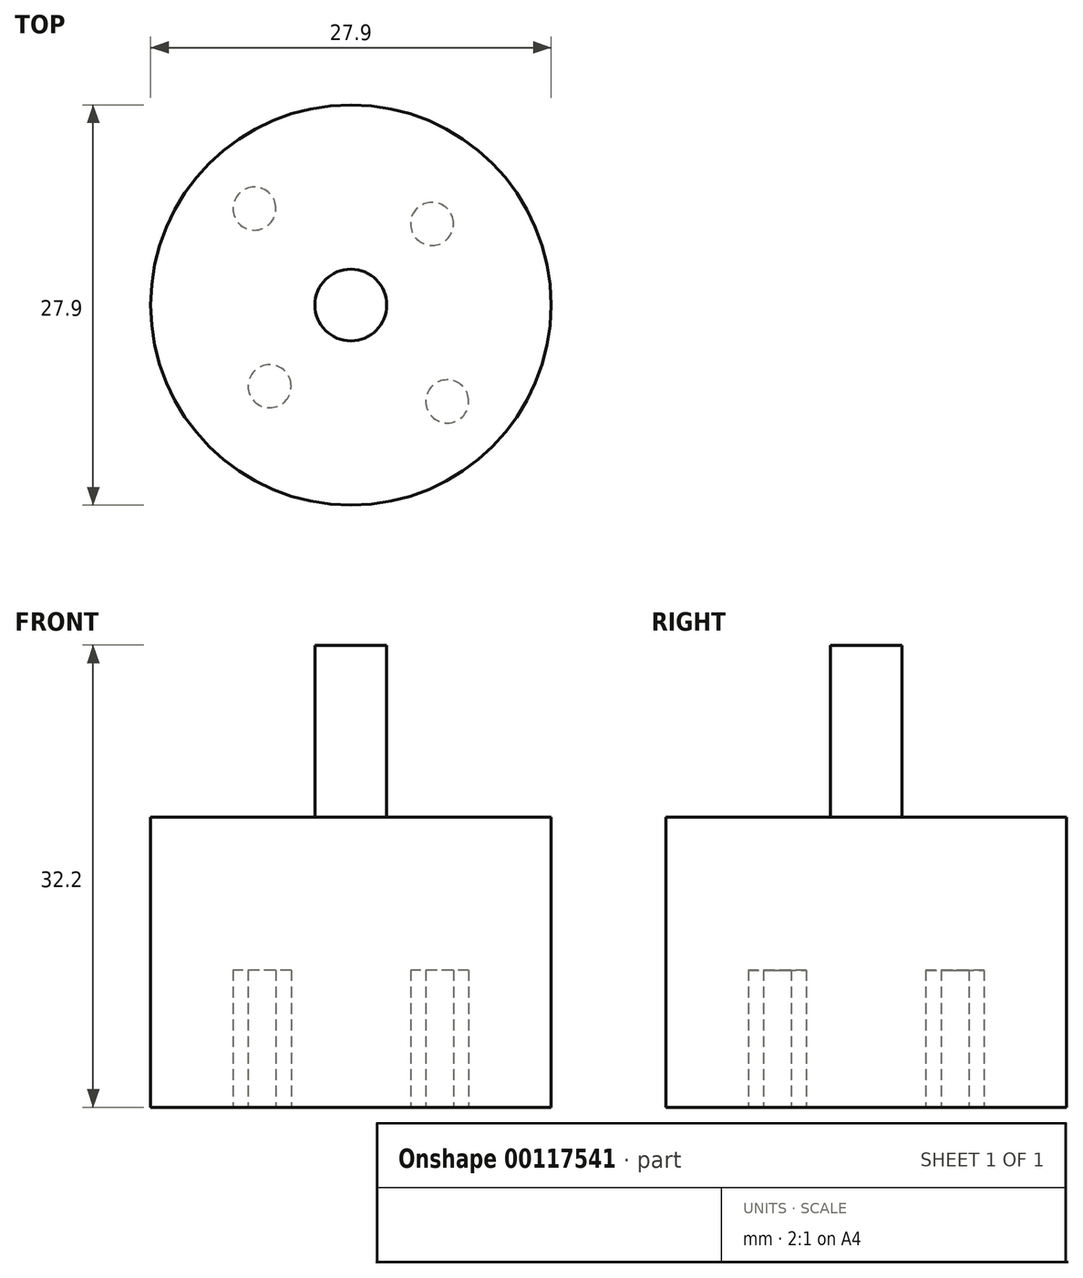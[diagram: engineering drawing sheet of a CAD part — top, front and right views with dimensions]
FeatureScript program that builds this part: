
annotation { "Feature Type Name" : "Feature", "Feature Type Description" : "" }
export const myFeature = defineFeature(function(context is Context, id is Id, definition is map)
    precondition{}
    {
        {
            var Q0;
            Q0=qCreatedBy(makeId("Front.planeOp"),FACE);
            var sketch = newSketch(context, id + "F0", { "sketchPlane" : qUnion([Q0])});
            skLineSegment(sketch, "E0", {"start": v(0, 15.85) * mm, "end": v(13.95, 15.85) * mm});
            skLineSegment(sketch, "E1", {"start": v(13.95, 15.85) * mm, "end": v(13.95, 36.06) * mm});
            skLineSegment(sketch, "E2", {"start": v(13.95, 36.06) * mm, "end": v(2.5, 36.05) * mm});
            skLineSegment(sketch, "E3", {"start": v(2.5, 36.05) * mm, "end": v(2.5, 48.05) * mm});
            skLineSegment(sketch, "E4", {"start": v(2.5, 48.05) * mm, "end": v(0, 48.05) * mm});
            skLineSegment(sketch, "E5", {"start": v(0, 48.05) * mm, "end": v(0, 15.85) * mm});
            skLineSegment(sketch, "E6", {"start": v(0, 15.85) * mm, "end": v(0, 15.85) * mm});
            skSolve(sketch);
        }
        {
            var Q0;
            {var subQ0=sQuery(id+"F0.wireOp",EDGE,"E1");Q0=makeQuery(id+"F0.imprint","IMPRINT",FACE,{"disambiguationData":[TD([[makeQuery(id+"F0.imprint","IMPRINT",EDGE,{"derivedFrom":subQ0}),1.0]])]});}
            var Q1;
            Q1=sQuery(id+"F0.wireOp",EDGE,"E5");
            revolve(context, id + "F1", {"entities" : qUnion([Q0]), "axis" : qUnion([Q1]), "revolveType" : RevolveType.FULL});
        }
        {
            var Q0;
            Q0=qCreatedBy(makeId("Top.planeOp"),FACE);
            var sketch = newSketch(context, id + "F2", { "sketchPlane" : qUnion([Q0])});
            skCircle(sketch, "E7", {"center": v(6.72, -6.72) * mm, "radius": 1.5 * mm});
            skCircle(sketch, "E8", {"center": v(-6.72, 6.72) * mm, "radius": 1.5 * mm});
            skLineSegment(sketch, "E9", {"start": v(-6.72, 6.72) * mm, "end": v(6.72, -6.72) * mm, "construction": true});
            skSolve(sketch);
        }
        {
            var Q0;
            Q0=qCreatedBy(makeId("Top.planeOp"),FACE);
            var sketch = newSketch(context, id + "F3", { "sketchPlane" : qUnion([Q0])});
            skCircle(sketch, "E10", {"center": v(-5.66, -5.66) * mm, "radius": 1.5 * mm});
            skCircle(sketch, "E11", {"center": v(5.66, 5.66) * mm, "radius": 1.5 * mm});
            skLineSegment(sketch, "E12", {"start": v(5.66, 5.66) * mm, "end": v(-5.66, -5.66) * mm, "construction": true});
            skSolve(sketch);
        }
        {
            var Q0;
            Q0 = qSketchRegion(id + "F2", true);
            extrude(context, id + "F4", {"entities" : qUnion([Q0]), "operationType" : NewBodyOperationType.REMOVE, "depth" : 25.4 * mm});
        }
        {
            var Q0;
            Q0 = qSketchRegion(id + "F3", true);
            extrude(context, id + "F5", {"entities" : qUnion([Q0]), "operationType" : NewBodyOperationType.REMOVE, "depth" : 25.4 * mm});
        }
    });
